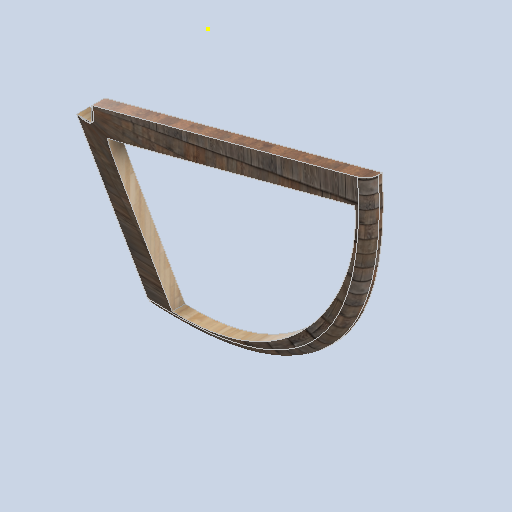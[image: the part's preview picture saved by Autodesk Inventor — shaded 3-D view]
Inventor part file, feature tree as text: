
AUTODESK INVENTOR PART (.ipt)
format: ipt  version: 2024.2 (Build 282272000, 272)  size: 296,960 bytes
history: native  units: in
note: dims shown in document units (in); Inventor stores cm internally (conversion verified against a paired STEP export)
features: sketch x12, plane x8, other x3
ambient origin geometry x8: Origin, YZ Plane, XZ Plane, XY Plane, X Axis, Y Axis, Z Axis, Center Point
bodies: Solid1 (feature_tree)
feature tree (23):
  other  "side_curve_corner_frame_MIR.ipt"
  other  "Solid1::side_curve_corner_frame_MIR.ipt"
  other  "TaggingFeature1"
  sketch  "Sketch1"  dims[d0=0.3937in]
  sketch  "Sketch2"
  sketch  "Sketch3"
  sketch  "Sketch4"
  sketch  "Sketch5"
  sketch  "Sketch6"
  sketch  "Sketch7"
  sketch  "Sketch8"
  sketch  "Sketch10"
  sketch  "Sketch11"
  sketch  "Sketch12"
  sketch  "Sketch14"
  plane  "Work Plane1"
  plane  "Work Plane2"
  plane  "Work Plane3"
  plane  "Work Plane4"
  plane  "Work Plane5"
  plane  "Work Plane6"
  plane  "Work Plane7"
  plane  "Work Plane8"
